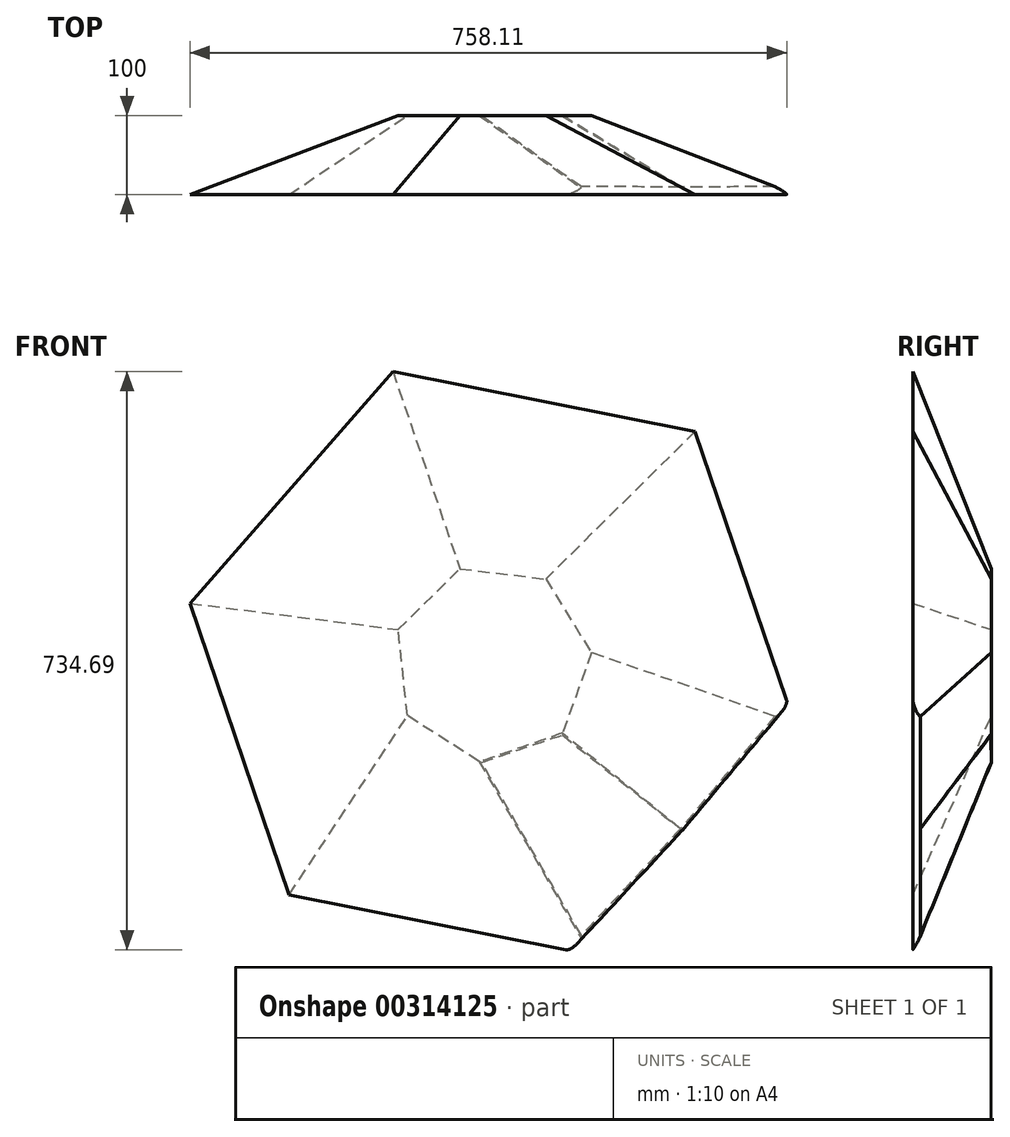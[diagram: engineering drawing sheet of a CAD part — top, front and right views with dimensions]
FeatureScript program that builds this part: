
annotation { "Feature Type Name" : "Feature", "Feature Type Description" : "" }
export const myFeature = defineFeature(function(context is Context, id is Id, definition is map)
    precondition{}
    {
        {
            var Q0;
            Q0=qCreatedBy(makeId("Front.planeOp"),FACE);
            cPlane(context, id + "F0", {"entities" : qUnion([Q0]), "cplaneType" : CPlaneType.OFFSET, "offset" : 100 * mm, "width" : 150 * mm, "height" : 150 * mm});
        }
        {
            var Q0;
            Q0=qCreatedBy(makeId("Front.planeOp"),FACE);
            var sketch = newSketch(context, id + "F1", { "sketchPlane" : qUnion([Q0])});
            skCircle(sketch, "E0.cCircle", {"center": v(0, 0) * mm, "radius": 114.17 * mm, "construction": true});
            skLineSegment(sketch, "E0.0", {"start": v(-41.07, 119.88) * mm, "end": v(68.12, 106.86) * mm});
            skLineSegment(sketch, "E0.1", {"start": v(68.12, 106.86) * mm, "end": v(126.02, 13.37) * mm});
            skLineSegment(sketch, "E0.2", {"start": v(126.02, 13.37) * mm, "end": v(89.02, -90.19) * mm});
            skLineSegment(sketch, "E0.3", {"start": v(89.02, -90.19) * mm, "end": v(-15, -125.83) * mm});
            skLineSegment(sketch, "E0.4", {"start": v(-15, -125.83) * mm, "end": v(-107.74, -66.72) * mm});
            skLineSegment(sketch, "E0.5", {"start": v(-107.74, -66.72) * mm, "end": v(-119.34, 42.63) * mm});
            skLineSegment(sketch, "E0.6", {"start": v(-119.34, 42.63) * mm, "end": v(-41.07, 119.88) * mm});
            skPoint(sketch, "E0.0.midPoint", {"position": v(13.52, 113.37) * mm});
            skSolve(sketch);
        }
        {
            var Q0;
            Q0=qCreatedBy(id+"F0.planeOp",FACE);
            var sketch = newSketch(context, id + "F2", { "sketchPlane" : qUnion([Q0])});
            skCircle(sketch, "E1.cCircle", {"center": v(0, 0) * mm, "radius": 338.94 * mm, "construction": true});
            skLineSegment(sketch, "E1.0", {"start": v(-383.93, 76) * mm, "end": v(-126.14, 370.5) * mm});
            skLineSegment(sketch, "E1.1", {"start": v(-126.14, 370.5) * mm, "end": v(257.78, 294.49) * mm});
            skLineSegment(sketch, "E1.2", {"start": v(257.78, 294.49) * mm, "end": v(383.93, -76) * mm});
            skLineSegment(sketch, "E1.3", {"start": v(383.93, -76) * mm, "end": v(126.14, -370.5) * mm});
            skLineSegment(sketch, "E1.4", {"start": v(126.14, -370.5) * mm, "end": v(-257.78, -294.49) * mm});
            skLineSegment(sketch, "E1.5", {"start": v(-257.78, -294.49) * mm, "end": v(-383.93, 76) * mm});
            skPoint(sketch, "E1.0.midPoint", {"position": v(-255.03, 223.25) * mm});
            skSolve(sketch);
        }
        {
            var Q0;
            Q0=makeQuery(id+"F2.imprint","IMPRINT",FACE,{"disambiguationData":[TD([[makeQuery(id+"F2.imprint","IMPRINT",EDGE,{"derivedFrom":sQuery(id+"F2.wireOp",EDGE,"E1.0")}),-1.0]])]});
            var Q1;
            Q1=makeQuery(id+"F1.imprint","IMPRINT",FACE,{"disambiguationData":[TD([[makeQuery(id+"F1.imprint","IMPRINT",EDGE,{"derivedFrom":sQuery(id+"F1.wireOp",EDGE,"E0.0")}),-1.0]])]});
            loft(context, id + "F3", {"sheetProfilesArray" : [{ "sheetProfileEntities" : qUnion([Q0]) }, { "sheetProfileEntities" : qUnion([Q1]) }]});
        }
        {
            var Q0;
            Q0=makeQuery(id+"F3.opLoft","SWEPT_FACE",FACE,{"disambiguationData":[OSD([sQuery(id+"F1.wireOp",EDGE,"E0.2"),sQuery(id+"F1.wireOp",EDGE,"E0.3"),sQuery(id+"F1.wireOp",EDGE,"E0.4"),sQuery(id+"F2.wireOp",EDGE,"E1.2"),sQuery(id+"F2.wireOp",EDGE,"E1.3"),sQuery(id+"F2.wireOp",EDGE,"E1.4")])]});
            fillet(context, id + "F4", {"entities" : qUnion([Q0]), "radius" : 5 * mm, "tangentPropagation" : true, "allowEdgeOverflow" : false});
        }
    });
